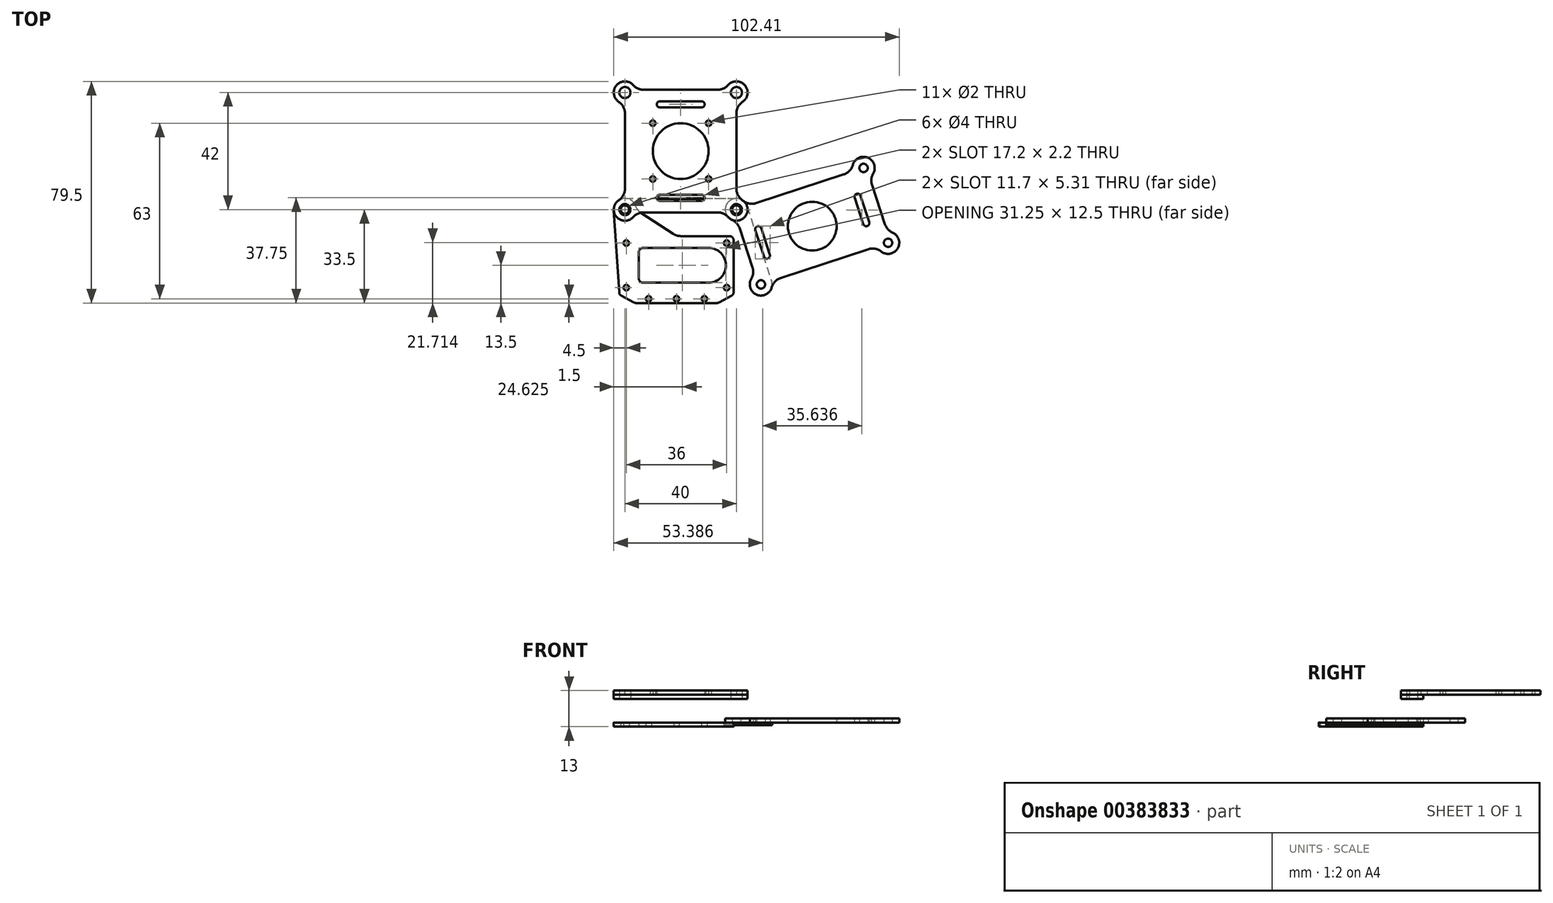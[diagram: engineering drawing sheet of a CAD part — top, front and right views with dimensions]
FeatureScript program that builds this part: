
annotation { "Feature Type Name" : "Feature", "Feature Type Description" : "" }
export const myFeature = defineFeature(function(context is Context, id is Id, definition is map)
    precondition{}
    {
        {
            var Q0;
            Q0=qCreatedBy(makeId("Top.planeOp"),FACE);
            var sketch = newSketch(context, id + "F0", { "sketchPlane" : qUnion([Q0])});
            skArc(sketch, "E0", {"start": v(0, -6.25) * mm, "mid": v(6.25, 0) * mm, "end": v(0, 6.25) * mm});
            skCircle(sketch, "E1", {"center": v(6.5, 8) * mm, "radius": 1 * mm});
            skLineSegment(sketch, "E2", {"start": v(6.5, 8) * mm, "end": v(-29.5, 8) * mm, "construction": true});
            skPoint(sketch, "E3", {"position": v(-11.5, 8) * mm});
            skCircle(sketch, "E4", {"center": v(-29.5, 8) * mm, "radius": 1 * mm});
            skCircle(sketch, "E5.MirrorC", {"center": v(-29.5, -8) * mm, "radius": 1 * mm});
            skCircle(sketch, "E6.MirrorC", {"center": v(6.5, -8) * mm, "radius": 1 * mm});
            skLineSegment(sketch, "E7.bottom", {"start": v(-32, 10.5) * mm, "end": v(9, 10.5) * mm});
            skLineSegment(sketch, "E7.top", {"start": v(-32, -10.5) * mm, "end": v(9, -10.5) * mm});
            skLineSegment(sketch, "E7.left", {"start": v(-32, 10.5) * mm, "end": v(-32, -10.5) * mm});
            skLineSegment(sketch, "E7.right", {"start": v(9, 10.5) * mm, "end": v(9, -10.5) * mm});
            skPoint(sketch, "E7.middle", {"position": v(-11.5, 0) * mm});
            skLineSegment(sketch, "E8", {"start": v(0, 0) * mm, "end": v(18.8, -6.84) * mm, "construction": true});
            skCircle(sketch, "E9", {"center": v(-30, 20) * mm, "radius": 1.5 * mm});
            skLineSegment(sketch, "E10", {"start": v(-30, 20) * mm, "end": v(10, 20) * mm, "construction": true});
            skLineSegment(sketch, "E11", {"start": v(10, 20) * mm, "end": v(18.8, -6.84) * mm, "construction": true});
            skCircle(sketch, "E12", {"center": v(10, 20) * mm, "radius": 1.5 * mm});
            skCircle(sketch, "E13", {"center": v(18.8, -6.84) * mm, "radius": 1.5 * mm});
            skCircle(sketch, "E14", {"center": v(18.8, -6.84) * mm, "radius": 4 * mm});
            skCircle(sketch, "E15", {"center": v(10, 20) * mm, "radius": 4 * mm});
            skLineSegment(sketch, "E16", {"start": v(10, 20) * mm, "end": v(13.8, 21.25) * mm, "construction": true});
            skLineSegment(sketch, "E17", {"start": v(13.8, 21.25) * mm, "end": v(22.6, -5.6) * mm});
            skLineSegment(sketch, "E18", {"start": v(10.26, 16) * mm, "end": v(16.64, -3.47) * mm});
            skCircle(sketch, "E19", {"center": v(-30, 20) * mm, "radius": 4 * mm});
            skLineSegment(sketch, "E20", {"start": v(-32, -10.5) * mm, "end": v(-34, 19.74) * mm});
            skLineSegment(sketch, "E21", {"start": v(-11.5, 10.5) * mm, "end": v(-26, 20) * mm});
            skLineSegment(sketch, "E22", {"start": v(0, 6.25) * mm, "end": v(-23.5, 6.25) * mm});
            skLineSegment(sketch, "E23", {"start": v(-25, 4.75) * mm, "end": v(-25, 0) * mm});
            skLineSegment(sketch, "E24.MirrorCS", {"start": v(-25, -4.75) * mm, "end": v(-25, 0) * mm});
            skLineSegment(sketch, "E25.MirrorCS", {"start": v(0, -6.25) * mm, "end": v(-23.5, -6.25) * mm});
            skPoint(sketch, "E26.visualSharp", {"position": v(-25, 6.25) * mm});
            skArc(sketch, "E26.filletArc", {"start": v(-23.5, 6.25) * mm, "mid": v(-24.56, 5.81) * mm, "end": v(-25, 4.75) * mm});
            skPoint(sketch, "E27.visualSharp", {"position": v(-25, -6.25) * mm});
            skArc(sketch, "E27.filletArc", {"start": v(-25, -4.75) * mm, "mid": v(-24.56, -5.81) * mm, "end": v(-23.5, -6.25) * mm});
            skPoint(sketch, "E28.visualSharp", {"position": v(0, 6.25) * mm});
            skLineSegment(sketch, "E28.filletArc", {"start": v(0, 6.25) * mm, "end": v(0, 6.25) * mm});
            skPoint(sketch, "E29.visualSharp", {"position": v(0, -6.25) * mm});
            skLineSegment(sketch, "E29.filletArc", {"start": v(0, -6.25) * mm, "end": v(0, -6.25) * mm});
            skLineSegment(sketch, "E30.bottom", {"start": v(-26.5, -10.5) * mm, "end": v(3.5, -10.5) * mm});
            skLineSegment(sketch, "E30.top", {"start": v(-26.5, -13.5) * mm, "end": v(3.5, -13.5) * mm});
            skLineSegment(sketch, "E30.left", {"start": v(-26.5, -10.5) * mm, "end": v(-26.5, -13.5) * mm});
            skLineSegment(sketch, "E30.right", {"start": v(3.5, -10.5) * mm, "end": v(3.5, -13.5) * mm});
            skPoint(sketch, "E30.middle", {"position": v(-11.5, -12) * mm});
            skLineSegment(sketch, "E31", {"start": v(-32, -10.5) * mm, "end": v(-26.5, -13.5) * mm});
            skLineSegment(sketch, "E32", {"start": v(3.5, -13.5) * mm, "end": v(9, -10.5) * mm});
            skCircle(sketch, "E33", {"center": v(-11.5, -12) * mm, "radius": 1 * mm});
            skCircle(sketch, "E34", {"center": v(-21.5, -12) * mm, "radius": 1 * mm});
            skLineSegment(sketch, "E35", {"start": v(-11.5, -10.5) * mm, "end": v(-11.5, -13.5) * mm, "construction": true});
            skCircle(sketch, "E36.MirrorC", {"center": v(-1.5, -12) * mm, "radius": 1 * mm});
            skSolve(sketch);
        }
        {
            var Q0;
            Q0 = qSketchRegion(id + "F0", true);
            extrude(context, id + "F1", {"entities" : qUnion([Q0]), "depth" : 1.5 * mm, "offsetDistance" : 25 * mm});
        }
        {
            var Q0;
            Q0=qCreatedBy(makeId("Top.planeOp"),FACE);
            cPlane(context, id + "F2", {"entities" : qUnion([Q0]), "cplaneType" : CPlaneType.OFFSET, "offset" : 10 * mm, "width" : 150 * mm, "height" : 150 * mm});
        }
        {
            var Q0;
            Q0=qCreatedBy(id+"F2.planeOp",FACE);
            var sketch = newSketch(context, id + "F3", { "sketchPlane" : qUnion([Q0])});
            skCircle(sketch, "E37.0", {"center": v(10, 20) * mm, "radius": 1.5 * mm});
            skCircle(sketch, "E38.0", {"center": v(-30, 20) * mm, "radius": 1.5 * mm});
            skArc(sketch, "E39", {"start": v(-30, 24) * mm, "mid": v(-33.16, 17.55) * mm, "end": v(-26.13, 19) * mm});
            skArc(sketch, "E40", {"start": v(6.13, 19) * mm, "mid": v(13.16, 17.55) * mm, "end": v(10, 24) * mm});
            skLineSegment(sketch, "E41", {"start": v(-30, 24) * mm, "end": v(10, 24) * mm});
            skLineSegment(sketch, "E42", {"start": v(-26.13, 19) * mm, "end": v(6.13, 19) * mm});
            skCircle(sketch, "E43", {"center": v(10, 20) * mm, "radius": 2 * mm});
            skCircle(sketch, "E44", {"center": v(-30, 20) * mm, "radius": 2 * mm});
            skSolve(sketch);
        }
        {
            var Q0;
            Q0 = qSketchRegion(id + "F3", true);
            extrude(context, id + "F4", {"entities" : qUnion([Q0]), "depth" : 1.5 * mm, "offsetDistance" : 25 * mm});
        }
        {
            var Q0;
            Q0=makeQuery(id+"F1.opExtrude","SWEPT_EDGE",EDGE,{"disambiguationData":[OSD([sQuery(id+"F0.wireOp",EDGE,"E15"),sQuery(id+"F0.wireOp",EDGE,"E18")])]});
            var Q1;
            Q1=makeQuery(id+"F1.opExtrude","SWEPT_EDGE",EDGE,{"disambiguationData":[OSD([sQuery(id+"F0.wireOp",EDGE,"E14"),sQuery(id+"F0.wireOp",EDGE,"E18")])]});
            var Q2;
            Q2=makeQuery(id+"F4.opExtrude","SWEPT_EDGE",EDGE,{"disambiguationData":[OSD([sQuery(id+"F3.wireOp",EDGE,"E39"),sQuery(id+"F3.wireOp",EDGE,"E42")])]});
            var Q3;
            Q3=makeQuery(id+"F4.opExtrude","SWEPT_EDGE",EDGE,{"disambiguationData":[OSD([sQuery(id+"F3.wireOp",EDGE,"E40"),sQuery(id+"F3.wireOp",EDGE,"E42")])]});
            var Q4;
            Q4=makeQuery(id+"F1.opExtrude","SWEPT_EDGE",EDGE,{"disambiguationData":[OSD([sQuery(id+"F0.wireOp",EDGE,"E19"),sQuery(id+"F0.wireOp",EDGE,"E21")])]});
            var Q5;
            Q5=makeQuery(id+"F1.opExtrude","SWEPT_EDGE",EDGE,{"disambiguationData":[OSD([sQuery(id+"F0.wireOp",EDGE,"E7.bottom"),sQuery(id+"F0.wireOp",EDGE,"E21")])]});
            fillet(context, id + "F5", {"entities" : qUnion([Q0, Q1, Q2, Q3, Q4, Q5]), "radius" : 5 * mm, "tangentPropagation" : true, "allowEdgeOverflow" : false});
        }
        {
            var Q0;
            Q0=makeQuery(id+"F1.opExtrude","SWEPT_EDGE",EDGE,{"disambiguationData":[OSD([sQuery(id+"F0.wireOp",EDGE,"E7.bottom"),sQuery(id+"F0.wireOp",EDGE,"E7.right")])]});
            var Q1;
            Q1=makeQuery(id+"F1.opExtrude","SWEPT_EDGE",EDGE,{"disambiguationData":[OSD([sQuery(id+"F0.wireOp",EDGE,"E7.top"),sQuery(id+"F0.wireOp",EDGE,"E7.left"),sQuery(id+"F0.wireOp",EDGE,"E20")])]});
            var Q2;
            Q2=makeQuery(id+"F1.opExtrude","SWEPT_EDGE",EDGE,{"disambiguationData":[OSD([sQuery(id+"F0.wireOp",EDGE,"E7.top"),sQuery(id+"F0.wireOp",EDGE,"E7.right")])]});
            var Q3;
            Q3=makeQuery(id+"F1.opExtrude","SWEPT_EDGE",EDGE,{"disambiguationData":[OSD([sQuery(id+"F0.wireOp",EDGE,"E30.top"),sQuery(id+"F0.wireOp",EDGE,"E30.left"),sQuery(id+"F0.wireOp",EDGE,"E31")])]});
            var Q4;
            Q4=makeQuery(id+"F1.opExtrude","SWEPT_EDGE",EDGE,{"disambiguationData":[OSD([sQuery(id+"F0.wireOp",EDGE,"E30.top"),sQuery(id+"F0.wireOp",EDGE,"E30.right"),sQuery(id+"F0.wireOp",EDGE,"E32")])]});
            fillet(context, id + "F6", {"entities" : qUnion([Q0, Q1, Q2, Q3, Q4]), "radius" : 1.5 * mm, "tangentPropagation" : true, "allowEdgeOverflow" : false});
        }
        {
            var Q0;
            Q0=makeQuery(id+"F1.opExtrude","CAP_FACE",FACE,{"disambiguationData":[OSD([sQuery(id+"F0.wireOp",EDGE,"E12"),sQuery(id+"F0.wireOp",EDGE,"E13"),sQuery(id+"F0.wireOp",EDGE,"E14"),sQuery(id+"F0.wireOp",EDGE,"E15"),sQuery(id+"F0.wireOp",EDGE,"E17"),sQuery(id+"F0.wireOp",EDGE,"E18")])],"isStart":true});
            extrude(context, id + "F7", {"entities" : qUnion([Q0]), "operationType" : NewBodyOperationType.REMOVE, "oppositeDirection" : true, "depth" : 0.5 * mm, "offsetDistance" : 25 * mm});
        }
        {
            var Q0;
            Q0=makeQuery(id+"F1.opExtrude","CAP_FACE",FACE,{"disambiguationData":[OSD([sQuery(id+"F0.wireOp",EDGE,"E12"),sQuery(id+"F0.wireOp",EDGE,"E13"),sQuery(id+"F0.wireOp",EDGE,"E14"),sQuery(id+"F0.wireOp",EDGE,"E15"),sQuery(id+"F0.wireOp",EDGE,"E17"),sQuery(id+"F0.wireOp",EDGE,"E18")])],"isStart":false});
            var sketch = newSketch(context, id + "F8", { "sketchPlane" : qUnion([Q0])});
            skLineSegment(sketch, "E45", {"start": v(13.45, 6.27) * mm, "end": v(37.2, 14.05) * mm, "construction": true});
            skLineSegment(sketch, "E46", {"start": v(37.2, 14.05) * mm, "end": v(41.6, 0.63) * mm, "construction": true});
            skLineSegment(sketch, "E47", {"start": v(22.6, -5.6) * mm, "end": v(41.6, 0.63) * mm});
            skPoint(sketch, "E48", {"position": v(18.8, -6.84) * mm});
            skLineSegment(sketch, "E49", {"start": v(18.8, -6.84) * mm, "end": v(22.6, -5.6) * mm, "construction": true});
            skLineSegment(sketch, "E50.MirrorCS", {"start": v(13.8, 21.25) * mm, "end": v(32.8, 27.47) * mm});
            skArc(sketch, "E51.0.0", {"start": v(13.8, 21.25) * mm, "mid": v(7.31, 22.96) * mm, "end": v(8.4, 16.34) * mm});
            skArc(sketch, "E51.0.1", {"start": v(8.4, 16.34) * mm, "mid": v(10.09, 15.12) * mm, "end": v(11.14, 13.31) * mm});
            skLineSegment(sketch, "E51.0.2", {"start": v(11.14, 13.31) * mm, "end": v(15.75, -0.78) * mm});
            skArc(sketch, "E51.0.3", {"start": v(15.75, -0.78) * mm, "mid": v(15.98, -2.85) * mm, "end": v(15.33, -4.84) * mm});
            skArc(sketch, "E51.0.4", {"start": v(15.33, -4.84) * mm, "mid": v(18.38, -10.82) * mm, "end": v(22.6, -5.6) * mm});
            skLineSegment(sketch, "E51.0.5", {"start": v(22.6, -5.6) * mm, "end": v(13.8, 21.25) * mm});
            skLineSegment(sketch, "E52.MirrorCS", {"start": v(58.65, 28.88) * mm, "end": v(63.27, 14.8) * mm});
            skArc(sketch, "E53.MirrorCS", {"start": v(59.08, 32.94) * mm, "mid": v(58.43, 30.96) * mm, "end": v(58.65, 28.88) * mm});
            skArc(sketch, "E54.MirrorCS", {"start": v(51.81, 33.7) * mm, "mid": v(56.03, 38.92) * mm, "end": v(59.08, 32.94) * mm});
            skLineSegment(sketch, "E55.MirrorCS", {"start": v(51.81, 33.7) * mm, "end": v(32.8, 27.47) * mm});
            skLineSegment(sketch, "E56.MirrorCS", {"start": v(64.4, 8.1) * mm, "end": v(60.6, 6.86) * mm, "construction": true});
            skLineSegment(sketch, "E57.MirrorCS", {"start": v(60.6, 6.86) * mm, "end": v(41.6, 0.63) * mm});
            skLineSegment(sketch, "E58.MirrorCS", {"start": v(60.96, 21.84) * mm, "end": v(37.2, 14.05) * mm, "construction": true});
            skArc(sketch, "E59.MirrorCS", {"start": v(63.27, 14.8) * mm, "mid": v(64.32, 12.99) * mm, "end": v(66.01, 11.77) * mm});
            skPoint(sketch, "E60.MirrorP", {"position": v(64.4, 8.1) * mm});
            skArc(sketch, "E61.MirrorCS", {"start": v(66.01, 11.77) * mm, "mid": v(67.1, 5.14) * mm, "end": v(60.6, 6.86) * mm});
            skLineSegment(sketch, "E62.MirrorCS", {"start": v(60.6, 6.86) * mm, "end": v(60.6, 6.86) * mm});
            skCircle(sketch, "E63.0", {"center": v(18.8, -6.84) * mm, "radius": 1.5 * mm});
            skCircle(sketch, "E64.MirrorC", {"center": v(64.4, 8.1) * mm, "radius": 1.5 * mm});
            skCircle(sketch, "E65", {"center": v(37.2, 14.05) * mm, "radius": 8.75 * mm});
            skLineSegment(sketch, "E66.trimOffspring", {"start": v(60.6, 6.86) * mm, "end": v(51.81, 33.7) * mm});
            skLineSegment(sketch, "E67.trimOffspring", {"start": v(13.8, 21.25) * mm, "end": v(13.8, 21.25) * mm});
            skCircle(sketch, "E68", {"center": v(53.47, 24.64) * mm, "radius": 1.1 * mm});
            skLineSegment(sketch, "E69", {"start": v(53.47, 24.64) * mm, "end": v(52.42, 24.3) * mm, "construction": true});
            skLineSegment(sketch, "E70", {"start": v(52.42, 24.3) * mm, "end": v(53.98, 19.55) * mm});
            skLineSegment(sketch, "E71", {"start": v(53.47, 24.64) * mm, "end": v(55.02, 19.9) * mm, "construction": true});
            skLineSegment(sketch, "E72.MirrorCS", {"start": v(54.51, 24.98) * mm, "end": v(56.07, 20.23) * mm});
            skLineSegment(sketch, "E73.MirrorCS", {"start": v(57.62, 15.48) * mm, "end": v(56.07, 20.23) * mm});
            skLineSegment(sketch, "E74.MirrorCS", {"start": v(55.53, 14.8) * mm, "end": v(53.98, 19.55) * mm});
            skCircle(sketch, "E75.MirrorC", {"center": v(56.58, 15.14) * mm, "radius": 1.1 * mm});
            skLineSegment(sketch, "E76.MirrorCS", {"start": v(56.58, 15.14) * mm, "end": v(55.02, 19.9) * mm, "construction": true});
            skLineSegment(sketch, "E77.MirrorCS", {"start": v(56.58, 15.14) * mm, "end": v(55.53, 14.8) * mm, "construction": true});
            skLineSegment(sketch, "E78.MirrorCS", {"start": v(17.83, 12.97) * mm, "end": v(18.87, 13.3) * mm, "construction": true});
            skLineSegment(sketch, "E79.MirrorCS", {"start": v(20.94, 3.46) * mm, "end": v(21.99, 3.8) * mm, "construction": true});
            skLineSegment(sketch, "E80.MirrorCS", {"start": v(19.9, 3.12) * mm, "end": v(18.34, 7.87) * mm});
            skCircle(sketch, "E81.MirrorC", {"center": v(17.83, 12.97) * mm, "radius": 1.1 * mm});
            skCircle(sketch, "E82.MirrorC", {"center": v(20.94, 3.46) * mm, "radius": 1.1 * mm});
            skLineSegment(sketch, "E83.MirrorCS", {"start": v(16.78, 12.62) * mm, "end": v(18.34, 7.87) * mm});
            skLineSegment(sketch, "E84.MirrorCS", {"start": v(18.87, 13.3) * mm, "end": v(20.43, 8.56) * mm});
            skLineSegment(sketch, "E85.MirrorCS", {"start": v(17.83, 12.97) * mm, "end": v(19.39, 8.21) * mm, "construction": true});
            skLineSegment(sketch, "E86.MirrorCS", {"start": v(20.94, 3.46) * mm, "end": v(19.39, 8.21) * mm, "construction": true});
            skLineSegment(sketch, "E87.MirrorCS", {"start": v(21.99, 3.8) * mm, "end": v(20.43, 8.56) * mm});
            skCircle(sketch, "E88.0", {"center": v(10, 20) * mm, "radius": 1.5 * mm});
            skCircle(sketch, "E89.MirrorC", {"center": v(55.61, 34.94) * mm, "radius": 1.5 * mm});
            skSolve(sketch);
        }
        {
            var Q0;
            Q0 = qSketchRegion(id + "F8", true);
            extrude(context, id + "F9", {"entities" : qUnion([Q0]), "depth" : 1.5 * mm, "offsetDistance" : 25 * mm});
        }
        {
            var Q0;
            Q0=makeQuery(id+"F4.opExtrude","CAP_FACE",FACE,{"disambiguationData":[OSD([sQuery(id+"F3.wireOp",EDGE,"E37.0"),sQuery(id+"F3.wireOp",EDGE,"E38.0"),sQuery(id+"F3.wireOp",EDGE,"E39"),sQuery(id+"F3.wireOp",EDGE,"E40"),sQuery(id+"F3.wireOp",EDGE,"E41"),sQuery(id+"F3.wireOp",EDGE,"E42")])],"isStart":false});
            var sketch = newSketch(context, id + "F10", { "sketchPlane" : qUnion([Q0])});
            skLineSegment(sketch, "E90", {"start": v(-10, 24) * mm, "end": v(-10, 41) * mm, "construction": true});
            skArc(sketch, "E91.0.0", {"start": v(-30, 24) * mm, "mid": v(-33.65, 18.37) * mm, "end": v(-27.02, 17.33) * mm});
            skArc(sketch, "E91.0.1", {"start": v(-27.02, 17.33) * mm, "mid": v(-25.33, 18.56) * mm, "end": v(-23.3, 19) * mm});
            skLineSegment(sketch, "E91.0.2", {"start": v(-23.3, 19) * mm, "end": v(3.3, 19) * mm});
            skArc(sketch, "E91.0.3", {"start": v(3.3, 19) * mm, "mid": v(5.33, 18.56) * mm, "end": v(7.02, 17.33) * mm});
            skArc(sketch, "E91.0.4", {"start": v(7.02, 17.33) * mm, "mid": v(13.65, 18.37) * mm, "end": v(10, 24) * mm});
            skLineSegment(sketch, "E91.0.5", {"start": v(10, 24) * mm, "end": v(-30, 24) * mm});
            skLineSegment(sketch, "E92", {"start": v(-10, 41) * mm, "end": v(10, 41) * mm, "construction": true});
            skArc(sketch, "E93.MirrorCS", {"start": v(-30, 58) * mm, "mid": v(-33.65, 63.63) * mm, "end": v(-27.02, 64.67) * mm});
            skArc(sketch, "E94.MirrorCS", {"start": v(-27.02, 64.67) * mm, "mid": v(-25.33, 63.44) * mm, "end": v(-23.3, 63) * mm});
            skLineSegment(sketch, "E95.MirrorCS", {"start": v(-23.3, 63) * mm, "end": v(3.3, 63) * mm});
            skArc(sketch, "E96.MirrorCS", {"start": v(3.3, 63) * mm, "mid": v(5.33, 63.44) * mm, "end": v(7.02, 64.67) * mm});
            skArc(sketch, "E97.MirrorCS", {"start": v(7.02, 64.67) * mm, "mid": v(13.65, 63.63) * mm, "end": v(10, 58) * mm});
            skLineSegment(sketch, "E98.MirrorCS", {"start": v(10, 58) * mm, "end": v(-30, 58) * mm});
            skLineSegment(sketch, "E99", {"start": v(10, 58) * mm, "end": v(10, 24) * mm});
            skLineSegment(sketch, "E100.MirrorCS", {"start": v(-30, 58) * mm, "end": v(-30, 24) * mm});
            skCircle(sketch, "E101", {"center": v(-10, 41) * mm, "radius": 10 * mm});
            skLineSegment(sketch, "E102", {"start": v(-30, 57.75) * mm, "end": v(10, 57.75) * mm, "construction": true});
            skCircle(sketch, "E103", {"center": v(-17.5, 57.75) * mm, "radius": 1.1 * mm});
            skLineSegment(sketch, "E104", {"start": v(-10, 56.65) * mm, "end": v(-17.5, 56.65) * mm});
            skLineSegment(sketch, "E105.MirrorCS", {"start": v(-10, 58.85) * mm, "end": v(-17.5, 58.85) * mm});
            skLineSegment(sketch, "E106.MirrorCS", {"start": v(-10, 58.85) * mm, "end": v(-2.5, 58.85) * mm});
            skCircle(sketch, "E107.MirrorC", {"center": v(-2.5, 57.75) * mm, "radius": 1.1 * mm});
            skLineSegment(sketch, "E108.MirrorCS", {"start": v(-10, 56.65) * mm, "end": v(-2.5, 56.65) * mm});
            skLineSegment(sketch, "E109.MirrorCS", {"start": v(-10, 23.15) * mm, "end": v(-17.5, 23.15) * mm});
            skCircle(sketch, "E110.MirrorC", {"center": v(-17.5, 24.25) * mm, "radius": 1.1 * mm});
            skLineSegment(sketch, "E111.MirrorCS", {"start": v(-10, 25.35) * mm, "end": v(-17.5, 25.35) * mm});
            skLineSegment(sketch, "E112.MirrorCS", {"start": v(-10, 23.15) * mm, "end": v(-2.5, 23.15) * mm});
            skLineSegment(sketch, "E113.MirrorCS", {"start": v(-10, 25.35) * mm, "end": v(-2.5, 25.35) * mm});
            skCircle(sketch, "E114.MirrorC", {"center": v(-2.5, 24.25) * mm, "radius": 1.1 * mm});
            skLineSegment(sketch, "E115.bottom", {"start": v(-20, 51) * mm, "end": v(0, 51) * mm, "construction": true});
            skLineSegment(sketch, "E115.top", {"start": v(-20, 31) * mm, "end": v(0, 31) * mm, "construction": true});
            skLineSegment(sketch, "E115.left", {"start": v(-20, 51) * mm, "end": v(-20, 31) * mm, "construction": true});
            skLineSegment(sketch, "E115.right", {"start": v(0, 51) * mm, "end": v(0, 31) * mm, "construction": true});
            skCircle(sketch, "E116", {"center": v(-20, 51) * mm, "radius": 1 * mm});
            skCircle(sketch, "E117.MirrorC", {"center": v(-20, 31) * mm, "radius": 1 * mm});
            skCircle(sketch, "E118.MirrorC", {"center": v(0, 51) * mm, "radius": 1 * mm});
            skCircle(sketch, "E119.MirrorC", {"center": v(0, 31) * mm, "radius": 1 * mm});
            skCircle(sketch, "E120.0", {"center": v(10, 20) * mm, "radius": 2 * mm});
            skCircle(sketch, "E121.0", {"center": v(-30, 20) * mm, "radius": 2 * mm});
            skCircle(sketch, "E122.MirrorC", {"center": v(-30, 62) * mm, "radius": 2 * mm});
            skCircle(sketch, "E123.MirrorC", {"center": v(10, 62) * mm, "radius": 2 * mm});
            skSolve(sketch);
        }
        {
            var Q0;
            Q0 = qSketchRegion(id + "F10", true);
            extrude(context, id + "F11", {"entities" : qUnion([Q0]), "depth" : 1.5 * mm, "offsetDistance" : 25 * mm});
        }
        {
            var Q0;
            Q0=makeQuery(id+"F9.opExtrude","SWEPT_EDGE",EDGE,{"disambiguationData":[OSD([sQuery(id+"F8.wireOp",EDGE,"E47"),sQuery(id+"F8.wireOp",EDGE,"E51.0.4"),sQuery(id+"F8.wireOp",EDGE,"E51.0.5")])]});
            var Q1;
            Q1=makeQuery(id+"F9.opExtrude","SWEPT_EDGE",EDGE,{"disambiguationData":[OSD([sQuery(id+"F8.wireOp",EDGE,"E57.MirrorCS"),sQuery(id+"F8.wireOp",EDGE,"E61.MirrorCS"),sQuery(id+"F8.wireOp",EDGE,"E66.trimOffspring")])]});
            var Q2;
            Q2=makeQuery(id+"F9.opExtrude","SWEPT_EDGE",EDGE,{"disambiguationData":[OSD([sQuery(id+"F8.wireOp",EDGE,"E54.MirrorCS"),sQuery(id+"F8.wireOp",EDGE,"E55.MirrorCS"),sQuery(id+"F8.wireOp",EDGE,"E66.trimOffspring")])]});
            var Q3;
            Q3=makeQuery(id+"F9.opExtrude","SWEPT_EDGE",EDGE,{"disambiguationData":[OSD([sQuery(id+"F8.wireOp",EDGE,"E50.MirrorCS"),sQuery(id+"F8.wireOp",EDGE,"E51.0.0"),sQuery(id+"F8.wireOp",EDGE,"E51.0.5")])]});
            var Q4;
            Q4=makeQuery(id+"F11.opExtrude","SWEPT_EDGE",EDGE,{"disambiguationData":[OSD([sQuery(id+"F10.wireOp",EDGE,"E97.MirrorCS"),sQuery(id+"F10.wireOp",EDGE,"E98.MirrorCS"),sQuery(id+"F10.wireOp",EDGE,"E99")])]});
            var Q5;
            Q5=makeQuery(id+"F11.opExtrude","SWEPT_EDGE",EDGE,{"disambiguationData":[OSD([sQuery(id+"F10.wireOp",EDGE,"E91.0.4"),sQuery(id+"F10.wireOp",EDGE,"E91.0.5"),sQuery(id+"F10.wireOp",EDGE,"E99")])]});
            var Q6;
            Q6=makeQuery(id+"F11.opExtrude","SWEPT_EDGE",EDGE,{"disambiguationData":[OSD([sQuery(id+"F10.wireOp",EDGE,"E91.0.0"),sQuery(id+"F10.wireOp",EDGE,"E91.0.5"),sQuery(id+"F10.wireOp",EDGE,"E100.MirrorCS")])]});
            var Q7;
            Q7=makeQuery(id+"F11.opExtrude","SWEPT_EDGE",EDGE,{"disambiguationData":[OSD([sQuery(id+"F10.wireOp",EDGE,"E93.MirrorCS"),sQuery(id+"F10.wireOp",EDGE,"E98.MirrorCS"),sQuery(id+"F10.wireOp",EDGE,"E100.MirrorCS")])]});
            fillet(context, id + "F12", {"entities" : qUnion([Q0, Q1, Q2, Q3, Q4, Q5, Q6, Q7]), "radius" : 5 * mm, "tangentPropagation" : true, "allowEdgeOverflow" : false});
        }
    });
